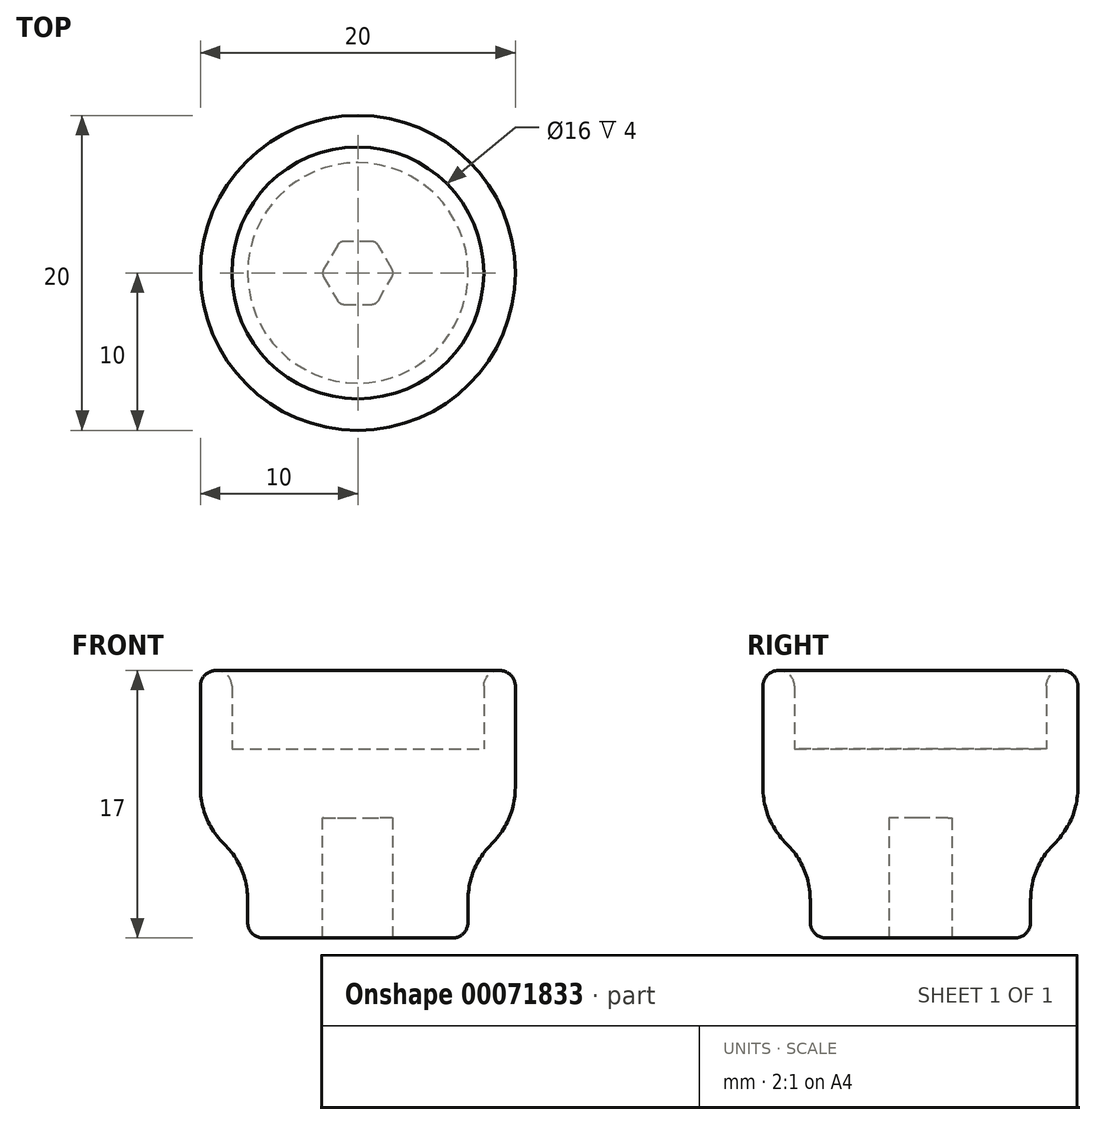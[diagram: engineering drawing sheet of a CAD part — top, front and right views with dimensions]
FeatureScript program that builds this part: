
annotation { "Feature Type Name" : "Feature", "Feature Type Description" : "" }
export const myFeature = defineFeature(function(context is Context, id is Id, definition is map)
    precondition{}
    {
        {
            var Q0;
            Q0=qCreatedBy(makeId("Front.planeOp"),FACE);
            var sketch = newSketch(context, id + "F0", { "sketchPlane" : qUnion([Q0])});
            skLineSegment(sketch, "E0", {"start": v(8, 0) * mm, "end": v(8, 5) * mm});
            skLineSegment(sketch, "E1", {"start": v(8, 5) * mm, "end": v(10, 5) * mm});
            skLineSegment(sketch, "E2", {"start": v(10, 5) * mm, "end": v(10, -12) * mm});
            skLineSegment(sketch, "E3", {"start": v(10, -12) * mm, "end": v(0, -12) * mm});
            skLineSegment(sketch, "E4", {"start": v(0, -12) * mm, "end": v(0, 0) * mm});
            skLineSegment(sketch, "E5", {"start": v(0, 0) * mm, "end": v(8, 0) * mm});
            skLineSegment(sketch, "E6", {"start": v(10, -5) * mm, "end": v(7, -5) * mm});
            skLineSegment(sketch, "E7", {"start": v(7, -5) * mm, "end": v(7, -12) * mm});
            skSolve(sketch);
        }
        {
            var Q0;
            Q0=makeQuery(id+"F0.imprint","IMPRINT",FACE,{"disambiguationData":[TD([[makeQuery(id+"F0.imprint","IMPRINT",EDGE,{"derivedFrom":sQuery(id+"F0.wireOp",EDGE,"E0")}),-1.0]])]});
            var Q1;
            Q1=sQuery(id+"F0.wireOp",EDGE,"E4");
            revolve(context, id + "F1", {"entities" : qUnion([Q0]), "axis" : qUnion([Q1]), "revolveType" : RevolveType.FULL});
        }
        {
            var Q0;
            Q0=makeQuery(id+"F1.opRevolve","SWEPT_FACE",FACE,{"disambiguationData":[OSD([sQuery(id+"F0.wireOp",EDGE,"E3")])]});
            var sketch = newSketch(context, id + "F2", { "sketchPlane" : qUnion([Q0])});
            skLineSegment(sketch, "E8.rect.bottom", {"start": v(3.17, 3.18) * mm, "end": v(-3.18, 3.17) * mm});
            skLineSegment(sketch, "E8.rect.top", {"start": v(3.18, -3.17) * mm, "end": v(-3.17, -3.18) * mm});
            skLineSegment(sketch, "E8.rect.left", {"start": v(3.17, 3.18) * mm, "end": v(3.18, -3.17) * mm});
            skLineSegment(sketch, "E8.rect.right", {"start": v(-3.18, 3.17) * mm, "end": v(-3.17, -3.18) * mm});
            skPoint(sketch, "E8.rect.middle", {"position": v(0, 0) * mm});
            skCircle(sketch, "E9.cCircle", {"center": v(0, 0) * mm, "radius": 2 * mm, "construction": true});
            skLineSegment(sketch, "E9.0", {"start": v(-1.15, 2) * mm, "end": v(1.15, 2) * mm});
            skLineSegment(sketch, "E9.1", {"start": v(1.15, 2) * mm, "end": v(2.3, 0) * mm});
            skLineSegment(sketch, "E9.2", {"start": v(2.3, 0) * mm, "end": v(1.15, -2) * mm});
            skLineSegment(sketch, "E9.3", {"start": v(1.15, -2) * mm, "end": v(-1.15, -2) * mm});
            skLineSegment(sketch, "E9.4", {"start": v(-1.15, -2) * mm, "end": v(-2.3, 0) * mm});
            skLineSegment(sketch, "E9.5", {"start": v(-2.3, 0) * mm, "end": v(-1.15, 2) * mm});
            skPoint(sketch, "E9.0.midPoint", {"position": v(0, 2) * mm});
            skSolve(sketch);
        }
        {
            var Q0;
            Q0=makeQuery(id+"F2.imprint","IMPRINT",FACE,{"disambiguationData":[TD([[makeQuery(id+"F2.imprint","IMPRINT",EDGE,{"derivedFrom":sQuery(id+"F2.wireOp",EDGE,"E9.0")}),-1.0]])]});
            extrude(context, id + "F3", {"entities" : qUnion([Q0]), "operationType" : NewBodyOperationType.REMOVE, "oppositeDirection" : true, "depth" : 7.62 * mm});
        }
        {
            var Q0;
            Q0=makeQuery(id+"F1.opRevolve","SWEPT_EDGE",EDGE,{"disambiguationData":[OSD([sQuery(id+"F0.wireOp",EDGE,"E6"),sQuery(id+"F0.wireOp",EDGE,"E7")])]});
            fillet(context, id + "F4", {"entities" : qUnion([Q0]), "radius" : 5 * mm, "tangentPropagation" : true, "allowEdgeOverflow" : false});
        }
        {
            var Q0;
            Q0=makeQuery(id+"F4.opFillet","BLEND_EDGE",EDGE,{"blendedFrom":[makeQuery(id+"F1.opRevolve","SWEPT_EDGE",EDGE,{"disambiguationData":[OSD([sQuery(id+"F0.wireOp",EDGE,"E6"),sQuery(id+"F0.wireOp",EDGE,"E7")])]}),makeQuery(id+"F1.opRevolve","SWEPT_FACE",FACE,{"disambiguationData":[OSD([sQuery(id+"F0.wireOp",EDGE,"E2")])]})],"blendedInto":[makeQuery(id+"F1.opRevolve","SWEPT_FACE",FACE,{"disambiguationData":[OSD([sQuery(id+"F0.wireOp",EDGE,"E2")])]})]});
            fillet(context, id + "F5", {"entities" : qUnion([Q0]), "radius" : 5 * mm, "tangentPropagation" : true, "allowEdgeOverflow" : false});
        }
        {
            var Q0;
            Q0=makeQuery(id+"F1.opRevolve","SWEPT_EDGE",EDGE,{"disambiguationData":[OSD([sQuery(id+"F0.wireOp",EDGE,"E1"),sQuery(id+"F0.wireOp",EDGE,"E2")])]});
            var Q1;
            Q1=makeQuery(id+"F1.opRevolve","SWEPT_EDGE",EDGE,{"disambiguationData":[OSD([sQuery(id+"F0.wireOp",EDGE,"E0"),sQuery(id+"F0.wireOp",EDGE,"E1")])]});
            var Q2;
            Q2=makeQuery(id+"F1.opRevolve","SWEPT_EDGE",EDGE,{"disambiguationData":[OSD([sQuery(id+"F0.wireOp",EDGE,"E3"),sQuery(id+"F0.wireOp",EDGE,"E7")])]});
            fillet(context, id + "F6", {"entities" : qUnion([Q0, Q1, Q2]), "radius" : 1 * mm, "tangentPropagation" : true, "allowEdgeOverflow" : false});
        }
        {
            var Q0;
            Q0=makeQuery(id+"F3.boolean.opBoolean","COPY",EDGE,{"derivedFrom":makeQuery(id+"F3.opExtrude","SWEPT_EDGE",EDGE,{"disambiguationData":[OSD([sQuery(id+"F2.wireOp",EDGE,"E9.4"),sQuery(id+"F2.wireOp",EDGE,"E9.5")])]})});
            var Q1;
            Q1=makeQuery(id+"F3.boolean.opBoolean","COPY",EDGE,{"derivedFrom":makeQuery(id+"F3.opExtrude","SWEPT_EDGE",EDGE,{"disambiguationData":[OSD([sQuery(id+"F2.wireOp",EDGE,"E9.0"),sQuery(id+"F2.wireOp",EDGE,"E9.5")])]})});
            var Q2;
            Q2=makeQuery(id+"F3.boolean.opBoolean","COPY",EDGE,{"derivedFrom":makeQuery(id+"F3.opExtrude","SWEPT_EDGE",EDGE,{"disambiguationData":[OSD([sQuery(id+"F2.wireOp",EDGE,"E9.0"),sQuery(id+"F2.wireOp",EDGE,"E9.1")])]})});
            var Q3;
            Q3=makeQuery(id+"F3.boolean.opBoolean","COPY",EDGE,{"derivedFrom":makeQuery(id+"F3.opExtrude","SWEPT_EDGE",EDGE,{"disambiguationData":[OSD([sQuery(id+"F2.wireOp",EDGE,"E9.1"),sQuery(id+"F2.wireOp",EDGE,"E9.2")])]})});
            var Q4;
            Q4=makeQuery(id+"F3.boolean.opBoolean","COPY",EDGE,{"derivedFrom":makeQuery(id+"F3.opExtrude","SWEPT_EDGE",EDGE,{"disambiguationData":[OSD([sQuery(id+"F2.wireOp",EDGE,"E9.2"),sQuery(id+"F2.wireOp",EDGE,"E9.3")])]})});
            var Q5;
            Q5=makeQuery(id+"F3.boolean.opBoolean","COPY",EDGE,{"derivedFrom":makeQuery(id+"F3.opExtrude","SWEPT_EDGE",EDGE,{"disambiguationData":[OSD([sQuery(id+"F2.wireOp",EDGE,"E9.3"),sQuery(id+"F2.wireOp",EDGE,"E9.4")])]})});
            fillet(context, id + "F7", {"entities" : qUnion([Q0, Q1, Q2, Q3, Q4, Q5]), "radius" : .5 * mm, "tangentPropagation" : true, "allowEdgeOverflow" : false});
        }
    });
